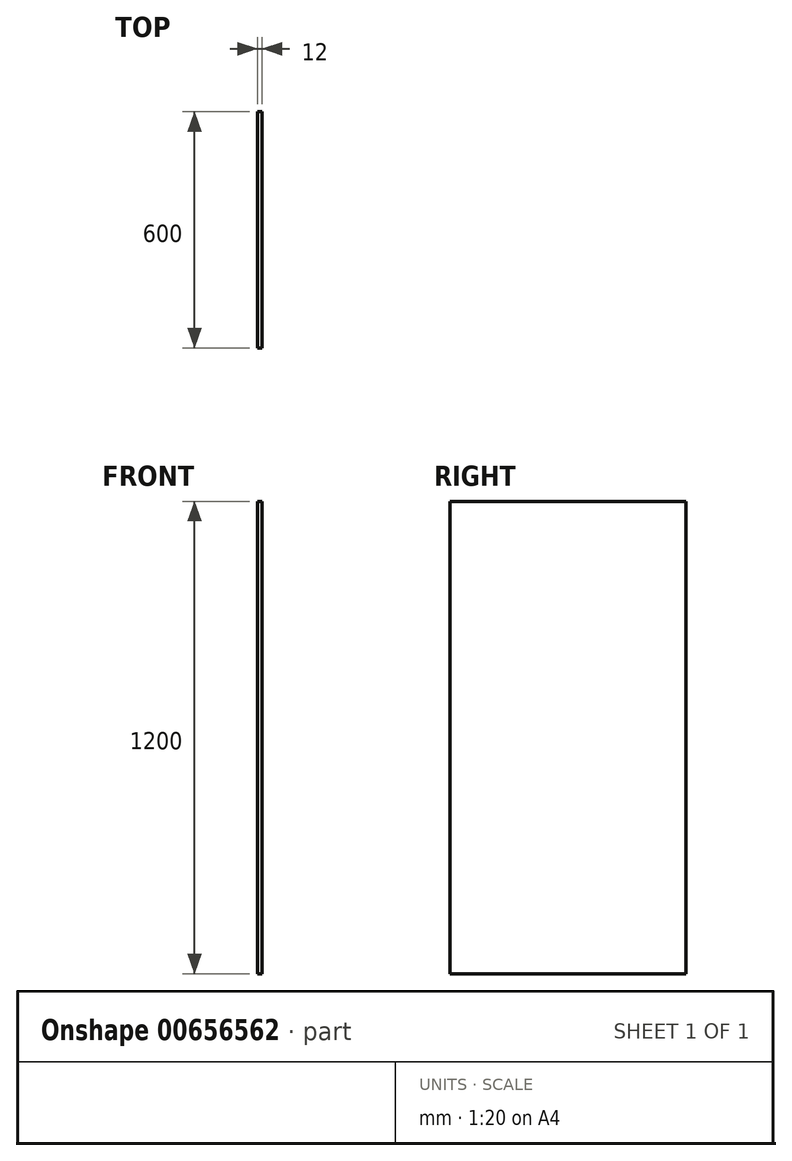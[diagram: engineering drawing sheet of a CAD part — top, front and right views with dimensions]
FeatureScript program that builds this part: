
annotation { "Feature Type Name" : "Feature", "Feature Type Description" : "" }
export const myFeature = defineFeature(function(context is Context, id is Id, definition is map)
    precondition{}
    {
        {
            var Q0;
            Q0=qCreatedBy(makeId("Right.planeOp"),FACE);
            var sketch = newSketch(context, id + "F0", { "sketchPlane" : qUnion([Q0])});
            skLineSegment(sketch, "E0.bottom", {"start": v(0, 0) * mm, "end": v(600, 0) * mm});
            skLineSegment(sketch, "E0.top", {"start": v(0, 1200) * mm, "end": v(600, 1200) * mm});
            skLineSegment(sketch, "E0.left", {"start": v(0, 0) * mm, "end": v(0, 1200) * mm});
            skLineSegment(sketch, "E0.right", {"start": v(600, 0) * mm, "end": v(600, 1200) * mm});
            skSolve(sketch);
        }
        {
            var Q0;
            Q0=makeQuery(id+"F0.imprint","IMPRINT",FACE,{"disambiguationData":[TD([[makeQuery(id+"F0.imprint","IMPRINT",EDGE,{"derivedFrom":sQuery(id+"F0.wireOp",EDGE,"E0.bottom")}),1.0]])]});
            extrude(context, id + "F1", {"entities" : qUnion([Q0]), "depth" : 12 * mm, "offsetDistance" : 25 * mm});
        }
    });
